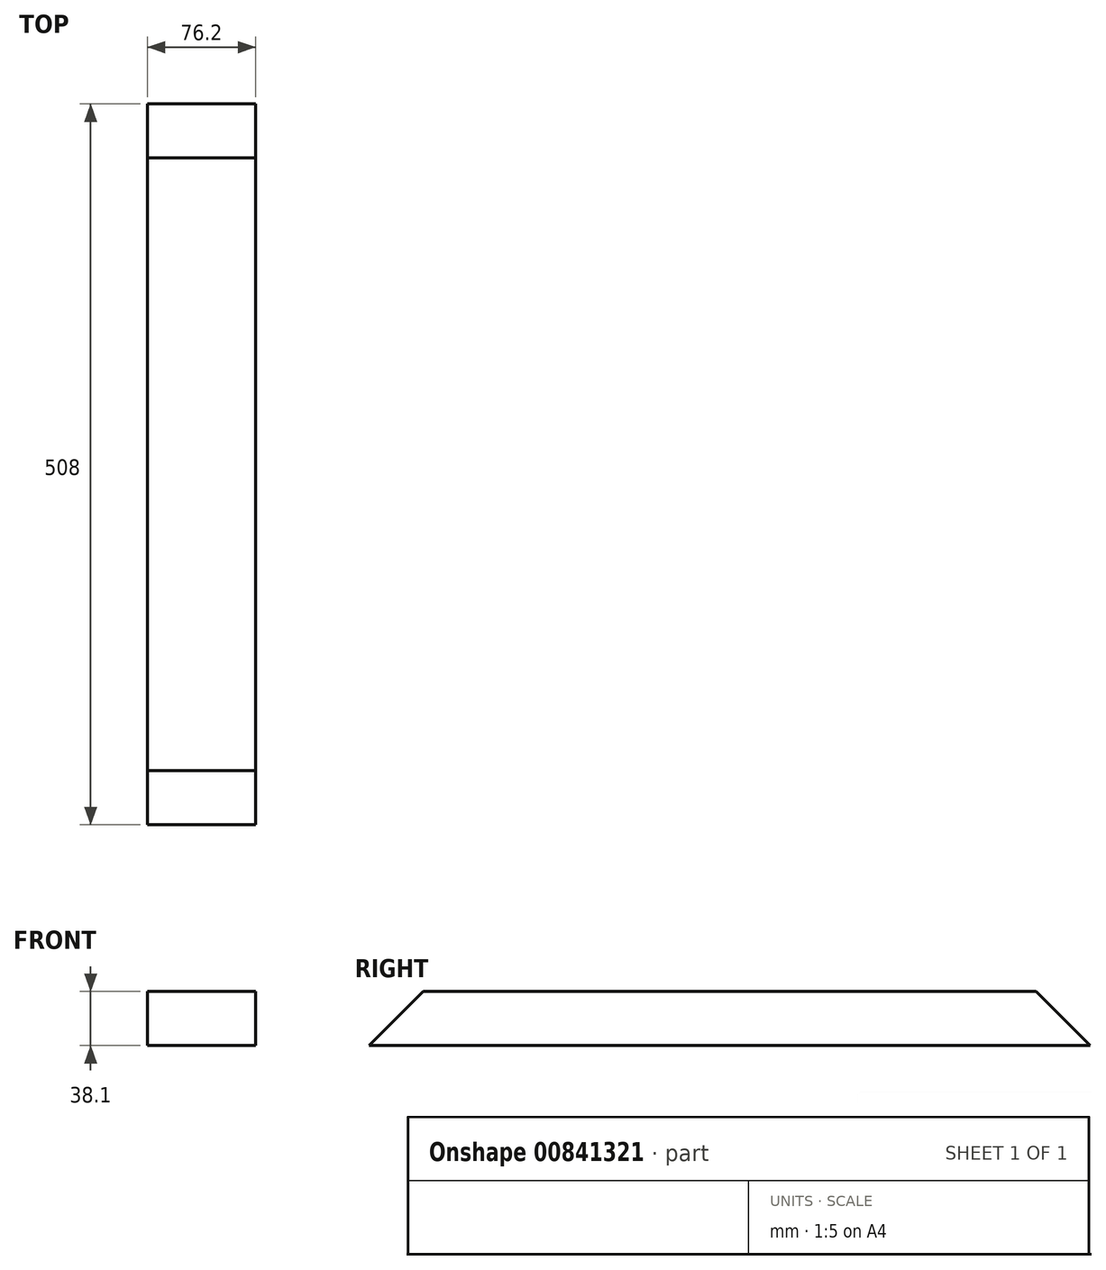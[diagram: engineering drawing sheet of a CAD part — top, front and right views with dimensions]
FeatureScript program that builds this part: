
annotation { "Feature Type Name" : "Feature", "Feature Type Description" : "" }
export const myFeature = defineFeature(function(context is Context, id is Id, definition is map)
    precondition{}
    {
        {
            var Q0;
            Q0=qCreatedBy(makeId("Front.planeOp"),FACE);
            var sketch = newSketch(context, id + "F0", { "sketchPlane" : qUnion([Q0])});
            skLineSegment(sketch, "E0.bottom", {"start": v(-38.1, 19.05) * mm, "end": v(38.1, 19.05) * mm});
            skLineSegment(sketch, "E0.top", {"start": v(-38.1, -19.05) * mm, "end": v(38.1, -19.05) * mm});
            skLineSegment(sketch, "E0.left", {"start": v(-38.1, 19.05) * mm, "end": v(-38.1, -19.05) * mm});
            skLineSegment(sketch, "E0.right", {"start": v(38.1, 19.05) * mm, "end": v(38.1, -19.05) * mm});
            skSolve(sketch);
        }
        {
            var Q0;
            Q0=qSketchRegion(id+"F0",true);
            extrude(context, id + "F1", {"entities" : qUnion([Q0]), "depth" : 254 * mm, "offsetDistance" : 25.4 * mm, "hasSecondDirection" : true, "secondDirectionOppositeDirection" : true, "secondDirectionDepth" : 254 * mm});
        }
        {
            var Q0;
            Q0=makeQuery(id+"F1.opExtrude","SWEPT_FACE",FACE,{"disambiguationData":[OSD([sQuery(id+"F0.wireOp",EDGE,"E0.left")])]});
            var sketch = newSketch(context, id + "F2", { "sketchPlane" : qUnion([Q0])});
            skLineSegment(sketch, "E1", {"start": v(-254, 19.05) * mm, "end": v(-254, -19.05) * mm});
            skLineSegment(sketch, "E2", {"start": v(-254, -19.05) * mm, "end": v(-215.9, 19.05) * mm});
            skLineSegment(sketch, "E3", {"start": v(-215.9, 19.05) * mm, "end": v(-254, 19.05) * mm});
            skLineSegment(sketch, "E4", {"start": v(254, -19.05) * mm, "end": v(254, 19.05) * mm});
            skLineSegment(sketch, "E5", {"start": v(254, 19.05) * mm, "end": v(215.9, 19.05) * mm});
            skLineSegment(sketch, "E6", {"start": v(215.9, 19.05) * mm, "end": v(254, -19.05) * mm});
            skSolve(sketch);
        }
        {
            var Q0;
            Q0=qSketchRegion(id+"F2",true);
            extrude(context, id + "F3", {"entities" : qUnion([Q0]), "operationType" : NewBodyOperationType.REMOVE, "endBound" : BoundingType.UP_TO_NEXT, "oppositeDirection" : true, "depth" : 25.4 * mm, "offsetDistance" : 25.4 * mm});
        }
    });
